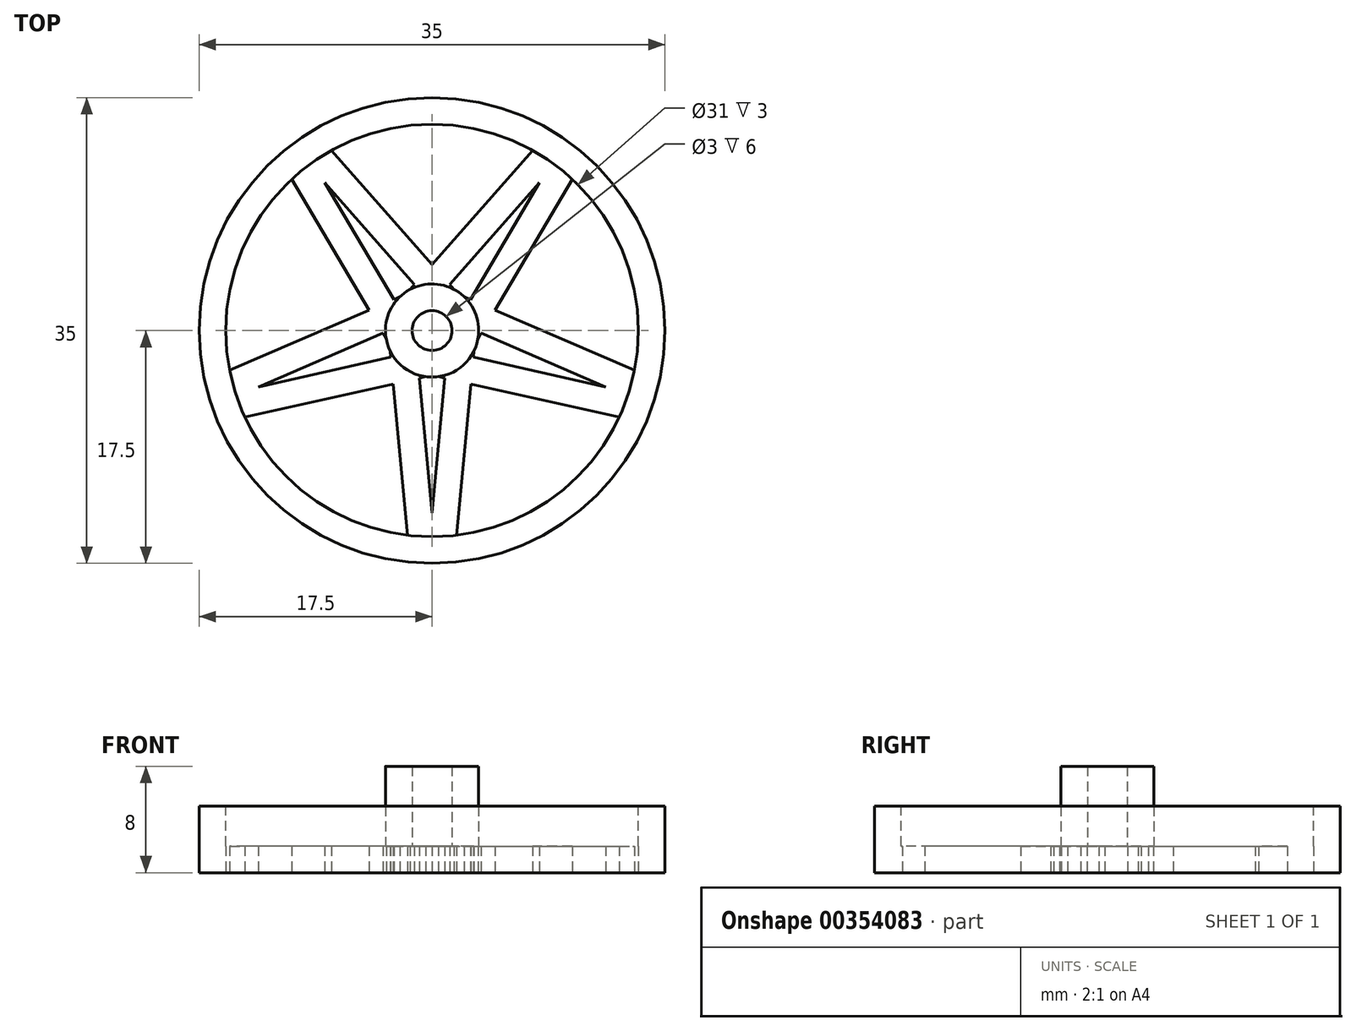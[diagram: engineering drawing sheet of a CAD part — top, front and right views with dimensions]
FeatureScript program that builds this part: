
annotation { "Feature Type Name" : "Feature", "Feature Type Description" : "" }
export const myFeature = defineFeature(function(context is Context, id is Id, definition is map)
    precondition{}
    {
        {
            var Q0;
            Q0=qCreatedBy(makeId("Top.planeOp"),FACE);
            var sketch = newSketch(context, id + "F0", { "sketchPlane" : qUnion([Q0])});
            skCircle(sketch, "E0", {"center": v(0, 0) * mm, "radius": 17.5 * mm});
            skSolve(sketch);
        }
        {
            var Q0;
            Q0=makeQuery(id+"F0.imprint","IMPRINT",FACE,{"disambiguationData":[TD([[makeQuery(id+"F0.imprint","IMPRINT",EDGE,{"derivedFrom":sQuery(id+"F0.wireOp",EDGE,"E0")}),1.0]])]});
            var Q1;
            Q1=sQuery(id+"F0.wireOp",EDGE,"E0");
            extrude(context, id + "F1", {"entities" : qUnion([Q0]), "surfaceEntities" : qUnion([Q1]), "depth" : 5 * mm});
        }
        {
            var Q0;
            Q0=makeQuery(id+"F1.opExtrude","CAP_FACE",FACE,{"disambiguationData":[OSD([sQuery(id+"F0.wireOp",EDGE,"E0")])],"isStart":false});
            var sketch = newSketch(context, id + "F2", { "sketchPlane" : qUnion([Q0])});
            skCircle(sketch, "E1", {"center": v(0, 0) * mm, "radius": 15.5 * mm});
            skSolve(sketch);
        }
        {
            var Q0;
            Q0=makeQuery(id+"F2.imprint","IMPRINT",FACE,{"disambiguationData":[TD([[makeQuery(id+"F2.imprint","IMPRINT",EDGE,{"derivedFrom":sQuery(id+"F2.wireOp",EDGE,"E1")}),1.0]])]});
            extrude(context, id + "F3", {"entities" : qUnion([Q0]), "operationType" : NewBodyOperationType.REMOVE, "oppositeDirection" : true, "depth" : 3 * mm});
        }
        {
            var Q0;
            Q0=makeQuery(id+"F3.boolean.opBoolean","COPY",FACE,{"derivedFrom":makeQuery(id+"F3.opExtrude","CAP_FACE",FACE,{"disambiguationData":[OSD([sQuery(id+"F2.wireOp",EDGE,"E1")])],"isStart":false})});
            var sketch = newSketch(context, id + "F4", { "sketchPlane" : qUnion([Q0])});
            skCircle(sketch, "E2", {"center": v(0, 0) * mm, "radius": 1.5 * mm});
            skCircle(sketch, "E3", {"center": v(0, 0) * mm, "radius": 3.5 * mm});
            skSolve(sketch);
        }
        {
            var Q0;
            Q0=makeQuery(id+"F4.imprint","IMPRINT",FACE,{"disambiguationData":[TD([[makeQuery(id+"F4.imprint","IMPRINT",EDGE,{"derivedFrom":sQuery(id+"F4.wireOp",EDGE,"E2")}),-1.0]])]});
            extrude(context, id + "F5", {"entities" : qUnion([Q0]), "operationType" : NewBodyOperationType.ADD, "depth" : 6 * mm});
        }
        {
            var Q0;
            Q0=makeQuery(id+"F1.opExtrude","CAP_FACE",FACE,{"disambiguationData":[OSD([sQuery(id+"F0.wireOp",EDGE,"E0")])],"isStart":true});
            var sketch = newSketch(context, id + "F6", { "sketchPlane" : qUnion([Q0])});
            skCircle(sketch, "E4", {"center": v(0, 0) * mm, "radius": 3.5 * mm});
            skCircle(sketch, "E5", {"center": v(0, 0) * mm, "radius": 18 * mm});
            skLineSegment(sketch, "E6", {"start": v(-3.15, 1.52) * mm, "end": v(-3.1, 2) * mm});
            skLineSegment(sketch, "E7.MirrorCS", {"start": v(3.15, 1.52) * mm, "end": v(3.1, 2) * mm});
            skLineSegment(sketch, "E8.0", {"start": v(-0.97, 3.36) * mm, "end": v(0, 13.72) * mm});
            skLineSegment(sketch, "E9.0", {"start": v(0.97, 3.36) * mm, "end": v(0, 13.72) * mm});
            skLineSegment(sketch, "E10.1.0", {"start": v(-0.47, 3.47) * mm, "end": v(-0.95, 3.57) * mm});
            skLineSegment(sketch, "E10.1.1", {"start": v(-2.9, 1.96) * mm, "end": v(-13.05, 4.24) * mm});
            skLineSegment(sketch, "E10.1.2", {"start": v(-3.5, 0.11) * mm, "end": v(-13.05, 4.24) * mm});
            skLineSegment(sketch, "E10.1.3", {"start": v(-2.42, -2.53) * mm, "end": v(-2.87, -2.34) * mm});
            skLineSegment(sketch, "E10.2.0", {"start": v(-3.44, 0.62) * mm, "end": v(-3.7, 0.2) * mm});
            skLineSegment(sketch, "E10.2.1", {"start": v(-2.76, -2.15) * mm, "end": v(-8.07, -11.1) * mm});
            skLineSegment(sketch, "E10.2.2", {"start": v(-1.19, -3.3) * mm, "end": v(-8.07, -11.1) * mm});
            skLineSegment(sketch, "E10.2.3", {"start": v(1.66, -3.08) * mm, "end": v(1.33, -3.46) * mm});
            skLineSegment(sketch, "E10.3.0", {"start": v(-1.66, -3.08) * mm, "end": v(-1.33, -3.46) * mm});
            skLineSegment(sketch, "E10.3.1", {"start": v(1.2, -3.3) * mm, "end": v(8.07, -11.1) * mm});
            skLineSegment(sketch, "E10.3.2", {"start": v(2.76, -2.15) * mm, "end": v(8.07, -11.1) * mm});
            skLineSegment(sketch, "E10.3.3", {"start": v(3.44, 0.62) * mm, "end": v(3.7, 0.2) * mm});
            skLineSegment(sketch, "E10.4.0", {"start": v(2.42, -2.53) * mm, "end": v(2.87, -2.34) * mm});
            skLineSegment(sketch, "E10.4.1", {"start": v(3.5, 0.11) * mm, "end": v(13.05, 4.24) * mm});
            skLineSegment(sketch, "E10.4.2", {"start": v(2.9, 1.96) * mm, "end": v(13.05, 4.24) * mm});
            skLineSegment(sketch, "E10.4.3", {"start": v(0.47, 3.47) * mm, "end": v(0.95, 3.57) * mm});
            skLineSegment(sketch, "E11.trimOffspring", {"start": v(-2.92, 4.01) * mm, "end": v(-1.61, 17.92) * mm});
            skLineSegment(sketch, "E12.trimOffspring", {"start": v(-2.92, 4.01) * mm, "end": v(-16.55, 7.07) * mm});
            skLineSegment(sketch, "E13.trimOffspring", {"start": v(2.92, 4.01) * mm, "end": v(16.55, 7.07) * mm});
            skLineSegment(sketch, "E14.trimOffspring", {"start": v(2.92, 4.01) * mm, "end": v(1.62, 17.92) * mm});
            skLineSegment(sketch, "E15.trimOffspring", {"start": v(4.72, -1.54) * mm, "end": v(11.84, -13.56) * mm});
            skLineSegment(sketch, "E16.trimOffspring", {"start": v(4.72, -1.54) * mm, "end": v(17.55, 4) * mm});
            skLineSegment(sketch, "E17.trimOffspring", {"start": v(0, -4.97) * mm, "end": v(-9.23, -15.46) * mm});
            skLineSegment(sketch, "E18.trimOffspring", {"start": v(0, -4.97) * mm, "end": v(9.23, -15.46) * mm});
            skLineSegment(sketch, "E19.trimOffspring", {"start": v(-4.72, -1.54) * mm, "end": v(-17.55, 4) * mm});
            skLineSegment(sketch, "E20.trimOffspring", {"start": v(-4.72, -1.54) * mm, "end": v(-11.84, -13.56) * mm});
            skCircle(sketch, "E21", {"center": v(0, 0) * mm, "radius": 15.5 * mm});
            skSolve(sketch);
        }
        {
            var Q0;
            {var subQ0=sQuery(id+"F6.wireOp",EDGE,"E12.trimOffspring");var subQ1=sQuery(id+"F6.wireOp",EDGE,"E11.trimOffspring");var subQ2=makeQuery(id+"F6.imprint","INTERSECT",VERTEX,{"derivedFrom":[subQ1,subQ0]});Q0=makeQuery(id+"F6.imprint","IMPRINT",FACE,{"disambiguationData":[TD([[makeQuery(id+"F6.imprint","IMPRINT",EDGE,{"disambiguationData":[TD([[subQ2,-1.0]])],"derivedFrom":subQ1}),1.0]])]});}
            var Q1;
            {var subQ0=sQuery(id+"F6.wireOp",EDGE,"E14.trimOffspring");var subQ1=sQuery(id+"F6.wireOp",EDGE,"E13.trimOffspring");var subQ2=makeQuery(id+"F6.imprint","INTERSECT",VERTEX,{"derivedFrom":[subQ1,subQ0]});Q1=makeQuery(id+"F6.imprint","IMPRINT",FACE,{"disambiguationData":[TD([[makeQuery(id+"F6.imprint","IMPRINT",EDGE,{"disambiguationData":[TD([[subQ2,-1.0]])],"derivedFrom":subQ1}),1.0]])]});}
            var Q2;
            {var subQ0=sQuery(id+"F6.wireOp",EDGE,"E16.trimOffspring");var subQ1=sQuery(id+"F6.wireOp",EDGE,"E15.trimOffspring");var subQ2=makeQuery(id+"F6.imprint","INTERSECT",VERTEX,{"derivedFrom":[subQ1,subQ0]});Q2=makeQuery(id+"F6.imprint","IMPRINT",FACE,{"disambiguationData":[TD([[makeQuery(id+"F6.imprint","IMPRINT",EDGE,{"disambiguationData":[TD([[subQ2,-1.0]])],"derivedFrom":subQ1}),1.0]])]});}
            var Q3;
            {var subQ0=sQuery(id+"F6.wireOp",EDGE,"E18.trimOffspring");var subQ1=sQuery(id+"F6.wireOp",EDGE,"E17.trimOffspring");var subQ2=makeQuery(id+"F6.imprint","INTERSECT",VERTEX,{"derivedFrom":[subQ1,subQ0]});Q3=makeQuery(id+"F6.imprint","IMPRINT",FACE,{"disambiguationData":[TD([[makeQuery(id+"F6.imprint","IMPRINT",EDGE,{"disambiguationData":[TD([[subQ2,-1.0]])],"derivedFrom":subQ1}),1.0]])]});}
            var Q4;
            {var subQ0=sQuery(id+"F6.wireOp",EDGE,"E20.trimOffspring");var subQ1=sQuery(id+"F6.wireOp",EDGE,"E19.trimOffspring");var subQ2=makeQuery(id+"F6.imprint","INTERSECT",VERTEX,{"derivedFrom":[subQ1,subQ0]});Q4=makeQuery(id+"F6.imprint","IMPRINT",FACE,{"disambiguationData":[TD([[makeQuery(id+"F6.imprint","IMPRINT",EDGE,{"disambiguationData":[TD([[subQ2,-1.0]])],"derivedFrom":subQ1}),1.0]])]});}
            var Q5;
            {var subQ1=sQuery(id+"F6.wireOp",EDGE,"E6");Q5=makeQuery(id+"F6.imprint","IMPRINT",FACE,{"disambiguationData":[TD([[makeQuery(id+"F6.imprint","IMPRINT",EDGE,{"derivedFrom":subQ1}),1.0]])]});}
            var Q6;
            {var subQ0=sQuery(id+"F6.wireOp",EDGE,"E10.1.0");Q6=makeQuery(id+"F6.imprint","IMPRINT",FACE,{"disambiguationData":[TD([[makeQuery(id+"F6.imprint","IMPRINT",EDGE,{"derivedFrom":subQ0}),-1.0]])]});}
            var Q7;
            {var subQ1=sQuery(id+"F6.wireOp",EDGE,"E7.MirrorCS");Q7=makeQuery(id+"F6.imprint","IMPRINT",FACE,{"disambiguationData":[TD([[makeQuery(id+"F6.imprint","IMPRINT",EDGE,{"derivedFrom":subQ1}),-1.0]])]});}
            var Q8;
            {var subQ1=sQuery(id+"F6.wireOp",EDGE,"E10.1.3");Q8=makeQuery(id+"F6.imprint","IMPRINT",FACE,{"disambiguationData":[TD([[makeQuery(id+"F6.imprint","IMPRINT",EDGE,{"derivedFrom":subQ1}),1.0]])]});}
            var Q9;
            {var subQ1=sQuery(id+"F6.wireOp",EDGE,"E10.2.3");Q9=makeQuery(id+"F6.imprint","IMPRINT",FACE,{"disambiguationData":[TD([[makeQuery(id+"F6.imprint","IMPRINT",EDGE,{"derivedFrom":subQ1}),1.0]])]});}
            extrude(context, id + "F7", {"entities" : qUnion([Q0, Q1, Q2, Q3, Q4, Q5, Q6, Q7, Q8, Q9]), "operationType" : NewBodyOperationType.REMOVE, "oppositeDirection" : true, "depth" : 2 * mm});
        }
    });
